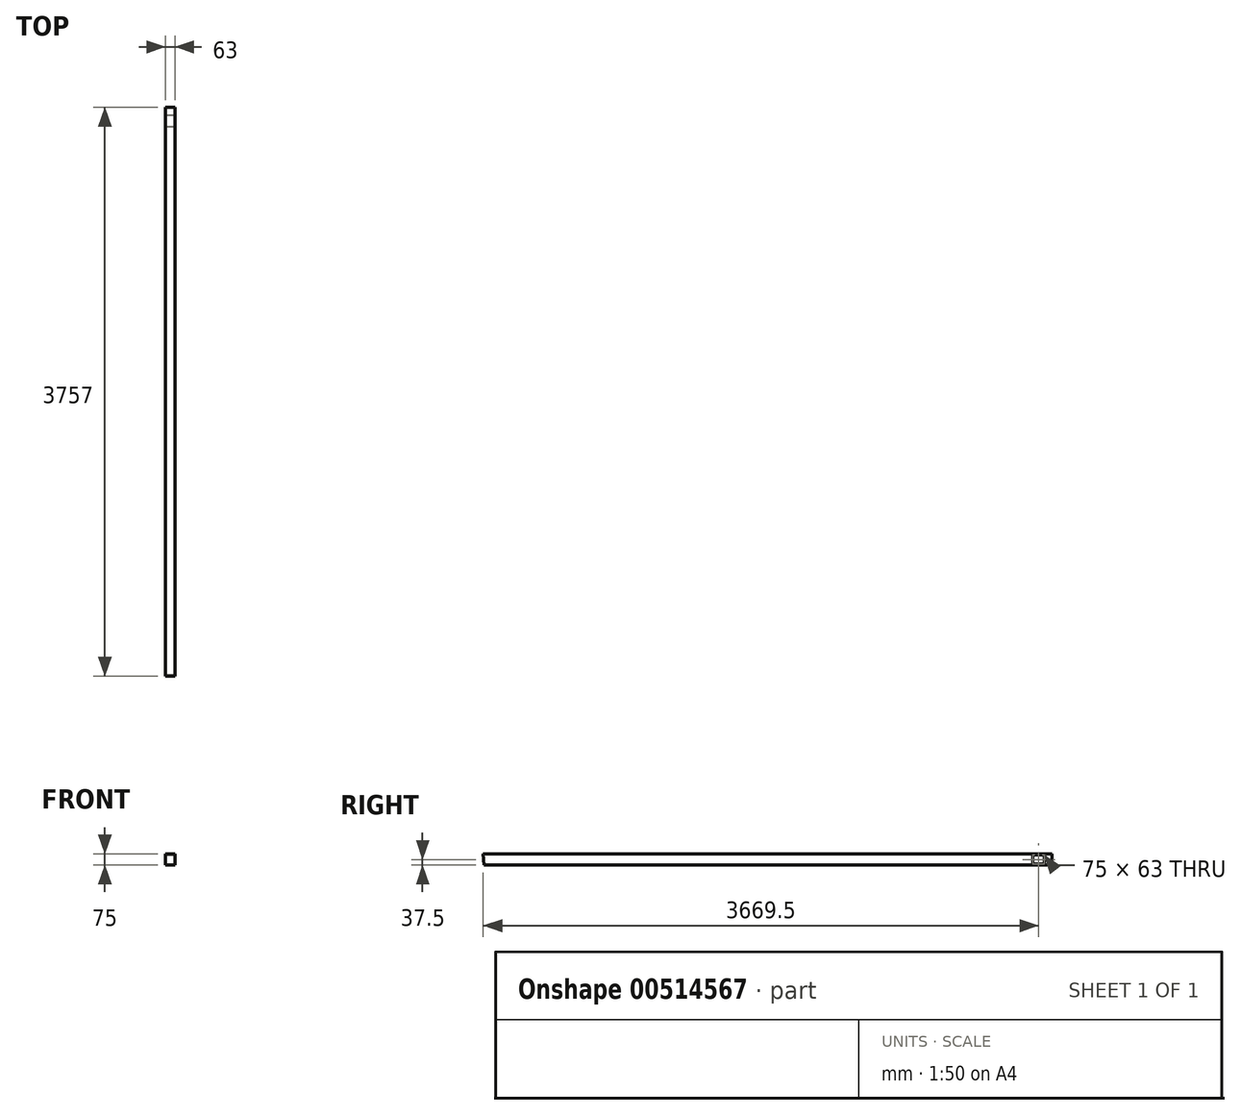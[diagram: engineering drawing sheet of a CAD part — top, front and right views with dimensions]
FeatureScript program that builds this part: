
annotation { "Feature Type Name" : "Feature", "Feature Type Description" : "" }
export const myFeature = defineFeature(function(context is Context, id is Id, definition is map)
    precondition{}
    {
        {
            var Q0;
            Q0=qCreatedBy(makeId("Front.planeOp"),FACE);
            var sketch = newSketch(context, id + "F0", { "sketchPlane" : qUnion([Q0])});
            skLineSegment(sketch, "E0.bottom", {"start": v(31.5, 37.5) * mm, "end": v(-31.5, 37.5) * mm});
            skLineSegment(sketch, "E0.top", {"start": v(31.5, -37.5) * mm, "end": v(-31.5, -37.5) * mm});
            skLineSegment(sketch, "E0.left", {"start": v(31.5, 37.5) * mm, "end": v(31.5, -37.5) * mm});
            skLineSegment(sketch, "E0.right", {"start": v(-31.5, 37.5) * mm, "end": v(-31.5, -37.5) * mm});
            skPoint(sketch, "E0.middle", {"position": v(0, 0) * mm});
            skSolve(sketch);
        }
        {
            var Q0;
            Q0 = qSketchRegion(id + "F0", true);
            extrude(context, id + "F1", {"entities" : qUnion([Q0]), "depth" : 3757 * mm});
        }
        {
            var Q0;
            Q0=makeQuery(id+"F1.opExtrude","SWEPT_FACE",FACE,{"disambiguationData":[OSD([sQuery(id+"F0.wireOp",EDGE,"E0.right")])]});
            var sketch = newSketch(context, id + "F2", { "sketchPlane" : qUnion([Q0])});
            skLineSegment(sketch, "E1", {"start": v(3757, 37.5) * mm, "end": v(3750.44, -37.5) * mm});
            skLineSegment(sketch, "E2", {"start": v(3750.44, -37.5) * mm, "end": v(3757, -37.5) * mm});
            skLineSegment(sketch, "E3", {"start": v(3757, -37.5) * mm, "end": v(3757, 37.5) * mm});
            skSolve(sketch);
        }
        {
            var Q0;
            Q0 = qSketchRegion(id + "F2", true);
            extrude(context, id + "F3", {"entities" : qUnion([Q0]), "operationType" : NewBodyOperationType.REMOVE, "endBound" : BoundingType.THROUGH_ALL, "oppositeDirection" : true, "depth" : 25 * mm});
        }
        {
            var Q0;
            Q0=makeQuery(id+"F1.opExtrude","SWEPT_FACE",FACE,{"disambiguationData":[OSD([sQuery(id+"F0.wireOp",EDGE,"E0.left")])]});
            var sketch = newSketch(context, id + "F4", { "sketchPlane" : qUnion([Q0])});
            skLineSegment(sketch, "E4.bottom", {"start": v(-50, 31.5) * mm, "end": v(-125, 31.5) * mm});
            skLineSegment(sketch, "E4.top", {"start": v(-50, -31.5) * mm, "end": v(-125, -31.5) * mm});
            skLineSegment(sketch, "E4.left", {"start": v(-50, 31.5) * mm, "end": v(-50, -31.5) * mm});
            skLineSegment(sketch, "E4.right", {"start": v(-125, 31.5) * mm, "end": v(-125, -31.5) * mm});
            skLineSegment(sketch, "E5", {"start": v(0, 0) * mm, "end": v(-308.12, 0) * mm, "construction": true});
            skSolve(sketch);
        }
        {
            var Q0;
            Q0 = qSketchRegion(id + "F4", true);
            extrude(context, id + "F5", {"entities" : qUnion([Q0]), "operationType" : NewBodyOperationType.REMOVE, "endBound" : BoundingType.THROUGH_ALL, "oppositeDirection" : true, "depth" : 25 * mm});
        }
    });
